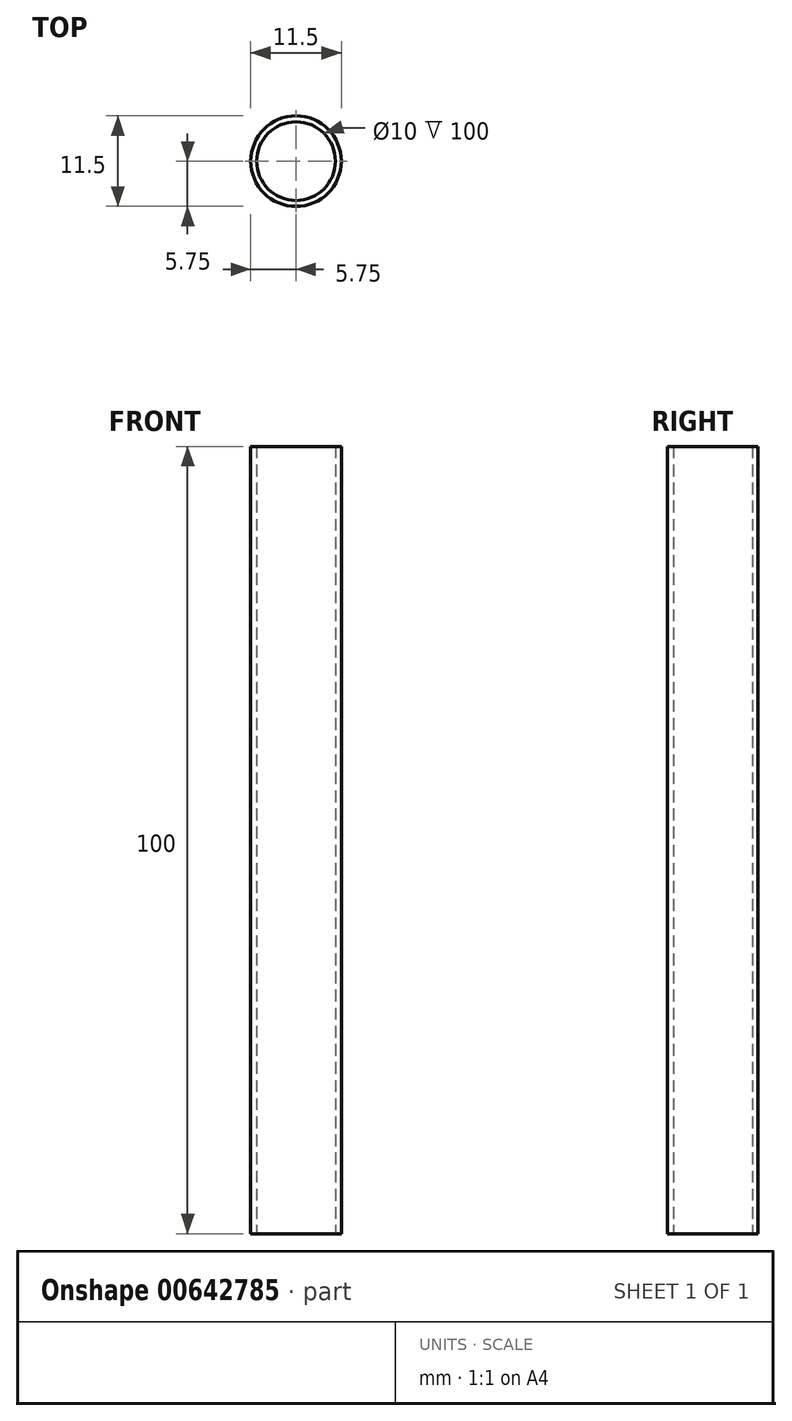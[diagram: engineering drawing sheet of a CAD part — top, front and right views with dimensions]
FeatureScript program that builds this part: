
annotation { "Feature Type Name" : "Feature", "Feature Type Description" : "" }
export const myFeature = defineFeature(function(context is Context, id is Id, definition is map)
    precondition{}
    {
        {
            var Q0;
            Q0=qCreatedBy(makeId("Top.planeOp"),FACE);
            var sketch = newSketch(context, id + "F0", { "sketchPlane" : qUnion([Q0])});
            skCircle(sketch, "E0", {"center": v(0, 0) * mm, "radius": 5 * mm});
            skCircle(sketch, "E1.0", {"center": v(0, 0) * mm, "radius": 5.75 * mm});
            skSolve(sketch);
        }
        {
            var Q0;
            Q0=makeQuery(id+"F0.imprint","IMPRINT",FACE,{"disambiguationData":[TD([[makeQuery(id+"F0.imprint","IMPRINT",EDGE,{"derivedFrom":sQuery(id+"F0.wireOp",EDGE,"E0")}),-1.0]])]});
            extrude(context, id + "F1", {"entities" : qUnion([Q0]), "depth" : 100 * mm, "offsetDistance" : 25 * mm});
        }
    });
